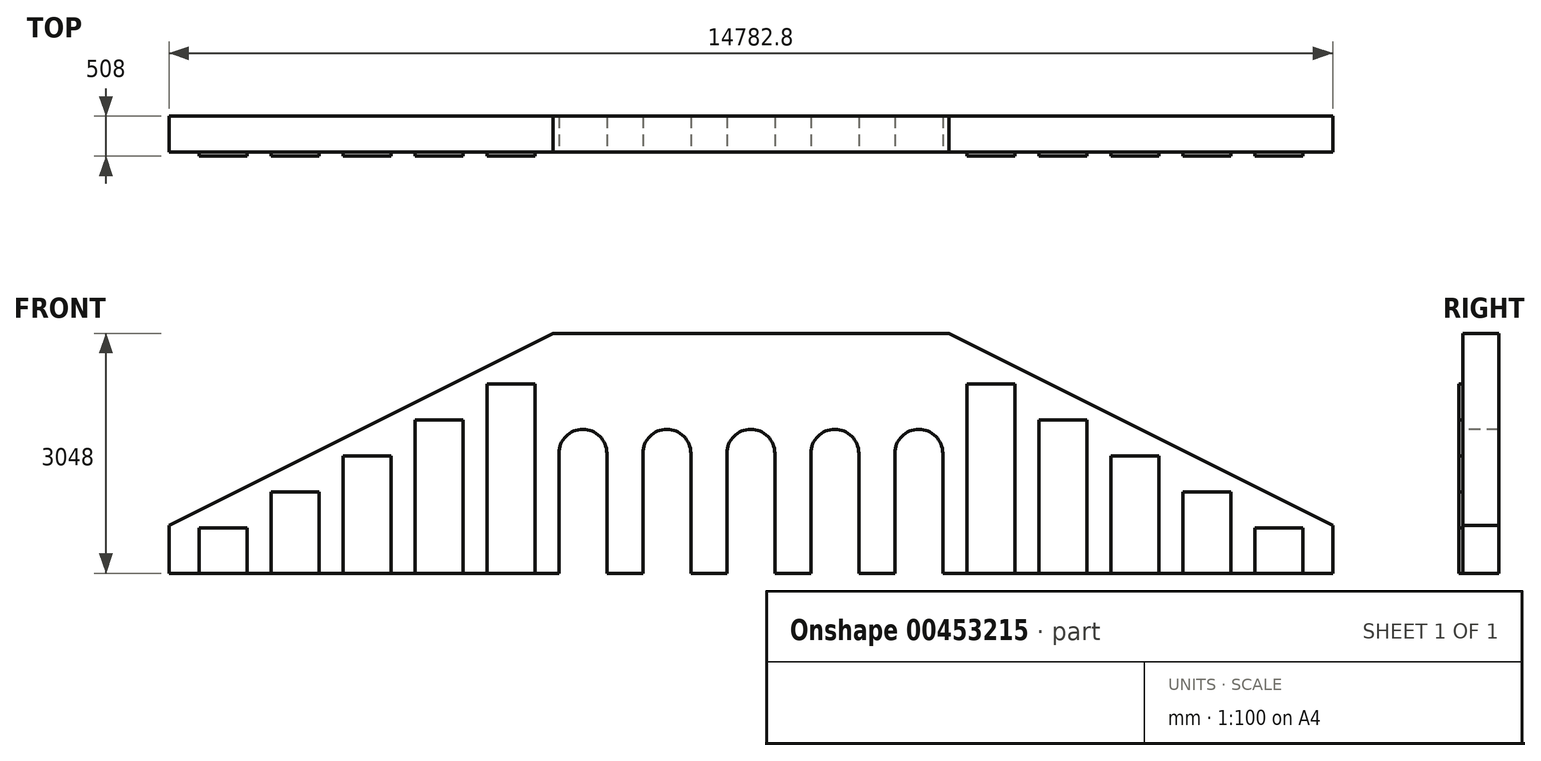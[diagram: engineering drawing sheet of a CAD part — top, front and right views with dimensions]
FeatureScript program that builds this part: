
annotation { "Feature Type Name" : "Feature", "Feature Type Description" : "" }
export const myFeature = defineFeature(function(context is Context, id is Id, definition is map)
    precondition{}
    {
        {
            var Q0;
            Q0=qCreatedBy(makeId("Front.planeOp"),FACE);
            var sketch = newSketch(context, id + "F0", { "sketchPlane" : qUnion([Q0])});
            skLineSegment(sketch, "E0", {"start": v(-7391.4, 0) * mm, "end": v(7391.4, 0) * mm});
            skLineSegment(sketch, "E1", {"start": v(7391.4, 0) * mm, "end": v(7391.4, 609.6) * mm});
            skLineSegment(sketch, "E2", {"start": v(7391.4, 609.6) * mm, "end": v(2514.6, 3048) * mm});
            skLineSegment(sketch, "E3", {"start": v(2514.6, 3048) * mm, "end": v(-2514.6, 3048) * mm});
            skLineSegment(sketch, "E4", {"start": v(-2514.6, 3048) * mm, "end": v(-7391.4, 609.6) * mm});
            skLineSegment(sketch, "E5", {"start": v(-7391.4, 609.6) * mm, "end": v(-7391.4, 0) * mm});
            skLineSegment(sketch, "E6.0", {"start": v(-2060.23, 3048) * mm, "end": v(-7391.4, 382.42) * mm, "construction": true});
            skSolve(sketch);
        }
        {
            var Q0;
            Q0=makeQuery(id+"F0.imprint","IMPRINT",FACE,{"disambiguationData":[TD([[makeQuery(id+"F0.imprint","IMPRINT",EDGE,{"derivedFrom":sQuery(id+"F0.wireOp",EDGE,"E0")}),1.0]])]});
            var sketch = newSketch(context, id + "F1", { "sketchPlane" : qUnion([Q0])});
            skLineSegment(sketch, "E7.bottom", {"start": v(-6096, 1030.12) * mm, "end": v(-5486.4, 1030.12) * mm});
            skLineSegment(sketch, "E7.top", {"start": v(-6096, 0) * mm, "end": v(-5486.4, 0) * mm});
            skLineSegment(sketch, "E7.left", {"start": v(-6096, 1030.12) * mm, "end": v(-6096, 0) * mm});
            skLineSegment(sketch, "E7.right", {"start": v(-5486.4, 1030.12) * mm, "end": v(-5486.4, 0) * mm});
            skLineSegment(sketch, "E8.bottom", {"start": v(-3352.8, 2401.72) * mm, "end": v(-2743.2, 2401.72) * mm});
            skLineSegment(sketch, "E8.top", {"start": v(-3352.8, 0) * mm, "end": v(-2743.2, 0) * mm});
            skLineSegment(sketch, "E8.left", {"start": v(-3352.8, 2401.72) * mm, "end": v(-3352.8, 0) * mm});
            skLineSegment(sketch, "E8.right", {"start": v(-2743.2, 2401.72) * mm, "end": v(-2743.2, 0) * mm});
            skLineSegment(sketch, "E9.bottom", {"start": v(-4267.2, 1944.52) * mm, "end": v(-3657.6, 1944.52) * mm});
            skLineSegment(sketch, "E9.top", {"start": v(-4267.2, 0) * mm, "end": v(-3657.6, 0) * mm});
            skLineSegment(sketch, "E9.left", {"start": v(-4267.2, 1944.52) * mm, "end": v(-4267.2, 0) * mm});
            skLineSegment(sketch, "E9.right", {"start": v(-3657.6, 1944.52) * mm, "end": v(-3657.6, 0) * mm});
            skPoint(sketch, "E10.oppositeSnap0", {"position": v(-3962.4, 0) * mm});
            skLineSegment(sketch, "E10.bottom", {"start": v(-5181.6, 1487.32) * mm, "end": v(-4572, 1487.32) * mm});
            skLineSegment(sketch, "E10.top", {"start": v(-5181.6, 0) * mm, "end": v(-4572, 0) * mm});
            skLineSegment(sketch, "E10.left", {"start": v(-5181.6, 1487.32) * mm, "end": v(-5181.6, 0) * mm});
            skLineSegment(sketch, "E10.right", {"start": v(-4572, 1487.32) * mm, "end": v(-4572, 0) * mm});
            skLineSegment(sketch, "E11", {"start": v(-6400.8, 0) * mm, "end": v(-6400.8, 572.92) * mm});
            skLineSegment(sketch, "E12", {"start": v(-6400.8, 572.92) * mm, "end": v(-7010.4, 572.92) * mm});
            skLineSegment(sketch, "E13", {"start": v(-7010.4, 572.92) * mm, "end": v(-7010.4, 0) * mm});
            skLineSegment(sketch, "E14", {"start": v(-7010.4, 0) * mm, "end": v(-6400.8, 0) * mm});
            skSolve(sketch);
        }
        {
            var Q0;
            Q0 = qSketchRegion(id + "F1", true);
            extrude(context, id + "F2", {"entities" : qUnion([Q0]), "depth" : 50.8 * mm});
        }
        {
            var Q0;
            Q0 = qSketchRegion(id + "F0", true);
            extrude(context, id + "F3", {"entities" : qUnion([Q0]), "oppositeDirection" : true, "depth" : 457.2 * mm});
        }
        {
            var Q0;
            Q0=makeQuery(id+"F2.opExtrude","SWEPT_BODY",BODY,{"disambiguationData":[OSD([sQuery(id+"F1.wireOp",EDGE,"E11"),sQuery(id+"F1.wireOp",EDGE,"E12"),sQuery(id+"F1.wireOp",EDGE,"E13"),sQuery(id+"F1.wireOp",EDGE,"E14")])]});
            var Q1;
            Q1=makeQuery(id+"F2.opExtrude","SWEPT_BODY",BODY,{"disambiguationData":[OSD([sQuery(id+"F1.wireOp",EDGE,"E7.bottom"),sQuery(id+"F1.wireOp",EDGE,"E7.top"),sQuery(id+"F1.wireOp",EDGE,"E7.left"),sQuery(id+"F1.wireOp",EDGE,"E7.right")])]});
            var Q2;
            Q2=makeQuery(id+"F2.opExtrude","SWEPT_BODY",BODY,{"disambiguationData":[OSD([sQuery(id+"F1.wireOp",EDGE,"E10.bottom"),sQuery(id+"F1.wireOp",EDGE,"E10.top"),sQuery(id+"F1.wireOp",EDGE,"E10.left"),sQuery(id+"F1.wireOp",EDGE,"E10.right")])]});
            var Q3;
            Q3=makeQuery(id+"F2.opExtrude","SWEPT_BODY",BODY,{"disambiguationData":[OSD([sQuery(id+"F1.wireOp",EDGE,"E9.bottom"),sQuery(id+"F1.wireOp",EDGE,"E9.top"),sQuery(id+"F1.wireOp",EDGE,"E9.left"),sQuery(id+"F1.wireOp",EDGE,"E9.right")])]});
            var Q4;
            Q4=makeQuery(id+"F2.opExtrude","SWEPT_BODY",BODY,{"disambiguationData":[OSD([sQuery(id+"F1.wireOp",EDGE,"E8.bottom"),sQuery(id+"F1.wireOp",EDGE,"E8.top"),sQuery(id+"F1.wireOp",EDGE,"E8.left"),sQuery(id+"F1.wireOp",EDGE,"E8.right")])]});
            var Q5;
            Q5=qCreatedBy(makeId("Right.planeOp"),FACE);
            mirror(context, id + "F4", {"operationType" : NewBodyOperationType.ADD, "entities" : qUnion([Q0, Q1, Q2, Q3, Q4]), "mirrorPlane" : qUnion([Q5])});
        }
        {
            var Q0;
            Q0=makeQuery(id+"F3.opExtrude","CAP_FACE",FACE,{"disambiguationData":[OSD([sQuery(id+"F0.wireOp",EDGE,"E0"),sQuery(id+"F0.wireOp",EDGE,"E1"),sQuery(id+"F0.wireOp",EDGE,"E2"),sQuery(id+"F0.wireOp",EDGE,"E3"),sQuery(id+"F0.wireOp",EDGE,"E4"),sQuery(id+"F0.wireOp",EDGE,"E5")])],"isStart":true});
            var sketch = newSketch(context, id + "F5", { "sketchPlane" : qUnion([Q0])});
            skLineSegment(sketch, "E15.bottom", {"start": v(-2438.4, 0) * mm, "end": v(-1828.8, 0) * mm});
            skLineSegment(sketch, "E15.left", {"start": v(-2438.4, 0) * mm, "end": v(-2438.4, 1524) * mm});
            skLineSegment(sketch, "E15.right", {"start": v(-1828.8, 0) * mm, "end": v(-1828.8, 1524) * mm});
            skArc(sketch, "E16", {"start": v(-2438.4, 1524) * mm, "mid": v(-2133.6, 1828.8) * mm, "end": v(-1828.8, 1524) * mm});
            skLineSegment(sketch, "E17.1.0.0", {"start": v(-1371.6, 0) * mm, "end": v(-1371.6, 1524) * mm});
            skLineSegment(sketch, "E17.1.0.1", {"start": v(-1371.6, 0) * mm, "end": v(-762, 0) * mm});
            skLineSegment(sketch, "E17.1.0.2", {"start": v(-762, 0) * mm, "end": v(-762, 1524) * mm});
            skArc(sketch, "E17.1.0.3", {"start": v(-1371.6, 1524) * mm, "mid": v(-1066.8, 1828.8) * mm, "end": v(-762, 1524) * mm});
            skLineSegment(sketch, "E17.2.0.0", {"start": v(-304.8, 0) * mm, "end": v(-304.8, 1524) * mm});
            skLineSegment(sketch, "E17.2.0.1", {"start": v(-304.8, 0) * mm, "end": v(304.8, 0) * mm});
            skLineSegment(sketch, "E17.2.0.2", {"start": v(304.8, 0) * mm, "end": v(304.8, 1524) * mm});
            skArc(sketch, "E17.2.0.3", {"start": v(-304.8, 1524) * mm, "mid": v(0, 1828.8) * mm, "end": v(304.8, 1524) * mm});
            skLineSegment(sketch, "E17.3.0.0", {"start": v(762, 0) * mm, "end": v(762, 1524) * mm});
            skLineSegment(sketch, "E17.3.0.1", {"start": v(762, 0) * mm, "end": v(1371.6, 0) * mm});
            skLineSegment(sketch, "E17.3.0.2", {"start": v(1371.6, 0) * mm, "end": v(1371.6, 1524) * mm});
            skArc(sketch, "E17.3.0.3", {"start": v(762, 1524) * mm, "mid": v(1066.8, 1828.8) * mm, "end": v(1371.6, 1524) * mm});
            skLineSegment(sketch, "E17.4.0.0", {"start": v(1828.8, 0) * mm, "end": v(1828.8, 1524) * mm});
            skLineSegment(sketch, "E17.4.0.1", {"start": v(1828.8, 0) * mm, "end": v(2438.4, 0) * mm});
            skLineSegment(sketch, "E17.4.0.2", {"start": v(2438.4, 0) * mm, "end": v(2438.4, 1524) * mm});
            skArc(sketch, "E17.4.0.3", {"start": v(1828.8, 1524) * mm, "mid": v(2133.6, 1828.8) * mm, "end": v(2438.4, 1524) * mm});
            skLineSegment(sketch, "E17.direction1", {"start": v(-2438.4, 0) * mm, "end": v(-1371.6, 0) * mm, "construction": true});
            skSolve(sketch);
        }
        {
            var Q0;
            Q0 = qSketchRegion(id + "F5", true);
            extrude(context, id + "F6", {"entities" : qUnion([Q0]), "operationType" : NewBodyOperationType.REMOVE, "endBound" : BoundingType.THROUGH_ALL, "oppositeDirection" : true, "depth" : 25.4 * mm});
        }
    });
